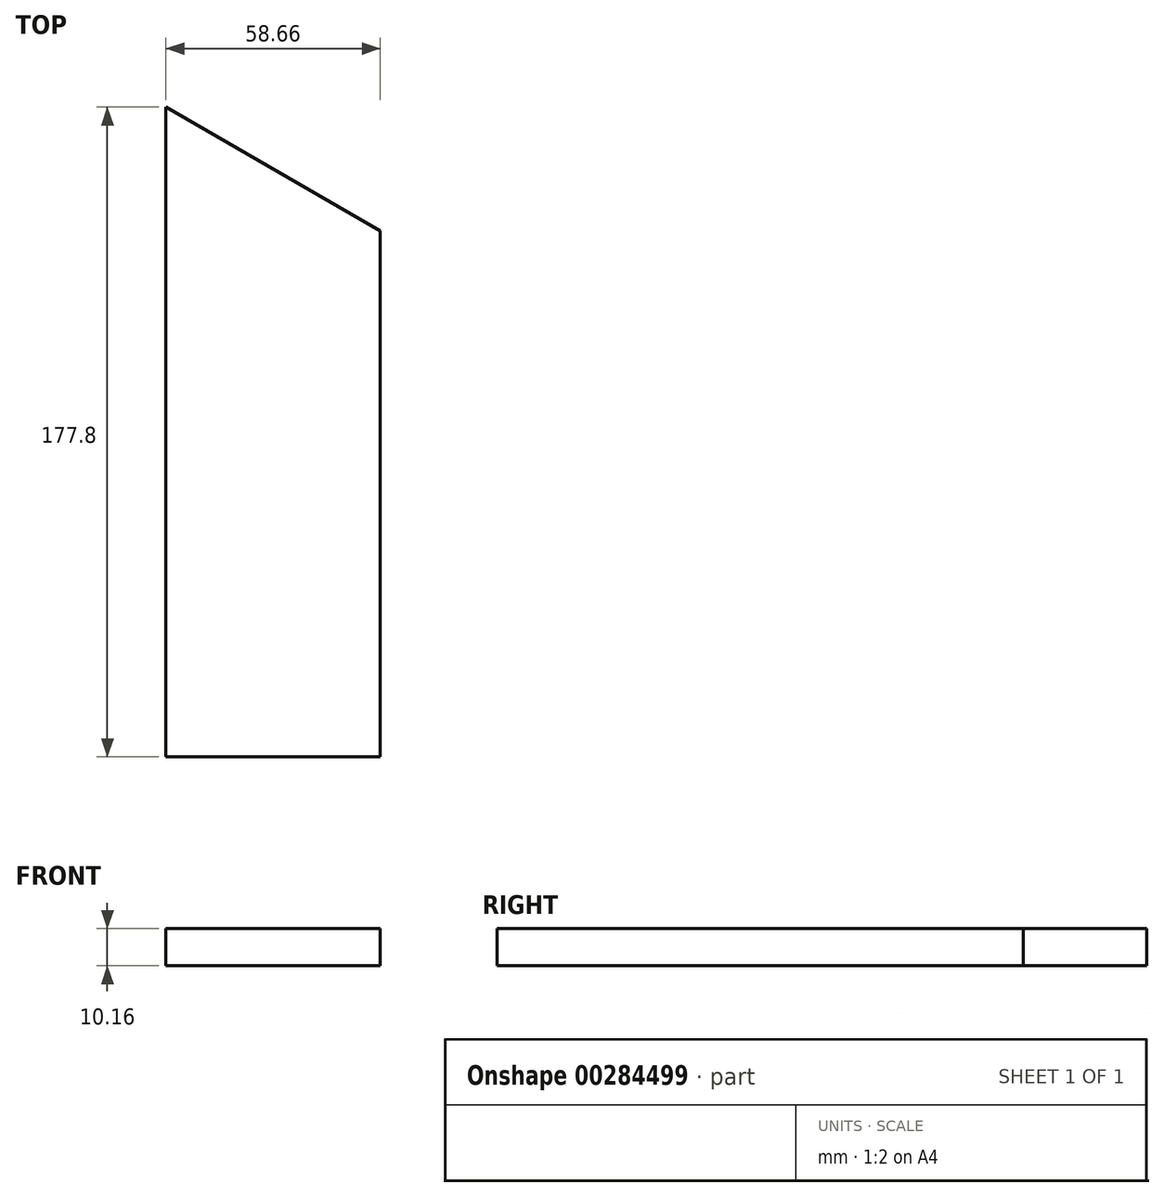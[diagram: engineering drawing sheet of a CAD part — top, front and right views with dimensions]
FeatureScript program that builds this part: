
annotation { "Feature Type Name" : "Feature", "Feature Type Description" : "" }
export const myFeature = defineFeature(function(context is Context, id is Id, definition is map)
    precondition{}
    {
        {
            var Q0;
            Q0=qCreatedBy(makeId("Top.planeOp"),FACE);
            var sketch = newSketch(context, id + "F0", { "sketchPlane" : qUnion([Q0])});
            skLineSegment(sketch, "E0", {"start": v(-23.12, 54.33) * mm, "end": v(-23.12, -123.47) * mm});
            skLineSegment(sketch, "E1", {"start": v(-23.12, -123.47) * mm, "end": v(35.54, -123.47) * mm});
            skLineSegment(sketch, "E2", {"start": v(35.54, -123.47) * mm, "end": v(35.54, 20.47) * mm});
            skLineSegment(sketch, "E3", {"start": v(35.54, 20.47) * mm, "end": v(-23.12, 54.33) * mm});
            skLineSegment(sketch, "E4", {"start": v(-23.12, -117.75) * mm, "end": v(35.54, -117.75) * mm, "construction": true});
            skLineSegment(sketch, "E5.bottom", {"start": v(-8.67, -117.75) * mm, "end": v(-1.05, -117.75) * mm});
            skLineSegment(sketch, "E6.top", {"start": v(8.8, -123.47) * mm, "end": v(25.31, -123.47) * mm});
            skLineSegment(sketch, "E7.bottom", {"start": v(13.4, -117.76) * mm, "end": v(21.02, -117.76) * mm});
            skLineSegment(sketch, "E8", {"start": v(-23.12, 47) * mm, "end": v(35.54, 13.13) * mm, "construction": true});
            skLineSegment(sketch, "E9", {"start": v(-11.14, 40.08) * mm, "end": v(-4.54, 36.27) * mm});
            skLineSegment(sketch, "E10", {"start": v(-41.2, 23.03) * mm, "end": v(-7.16, 81.98) * mm, "construction": true});
            skLineSegment(sketch, "E11", {"start": v(18.57, -8.92) * mm, "end": v(55.65, 55.31) * mm, "construction": true});
            skLineSegment(sketch, "E12.top", {"start": v(10.61, 27.52) * mm, "end": v(17.21, 23.71) * mm});
            skSolve(sketch);
        }
        {
            var Q0;
            {var subQ24=sQuery(id+"F0.wireOp",EDGE,"E0");Q0=makeQuery(id+"F0.imprint","IMPRINT",FACE,{"disambiguationData":[TD([[makeQuery(id+"F0.imprint","IMPRINT",EDGE,{"derivedFrom":subQ24}),1.0]])]});}
            extrude(context, id + "F1", {"entities" : qUnion([Q0]), "depth" : 10.16 * mm});
        }
    });
